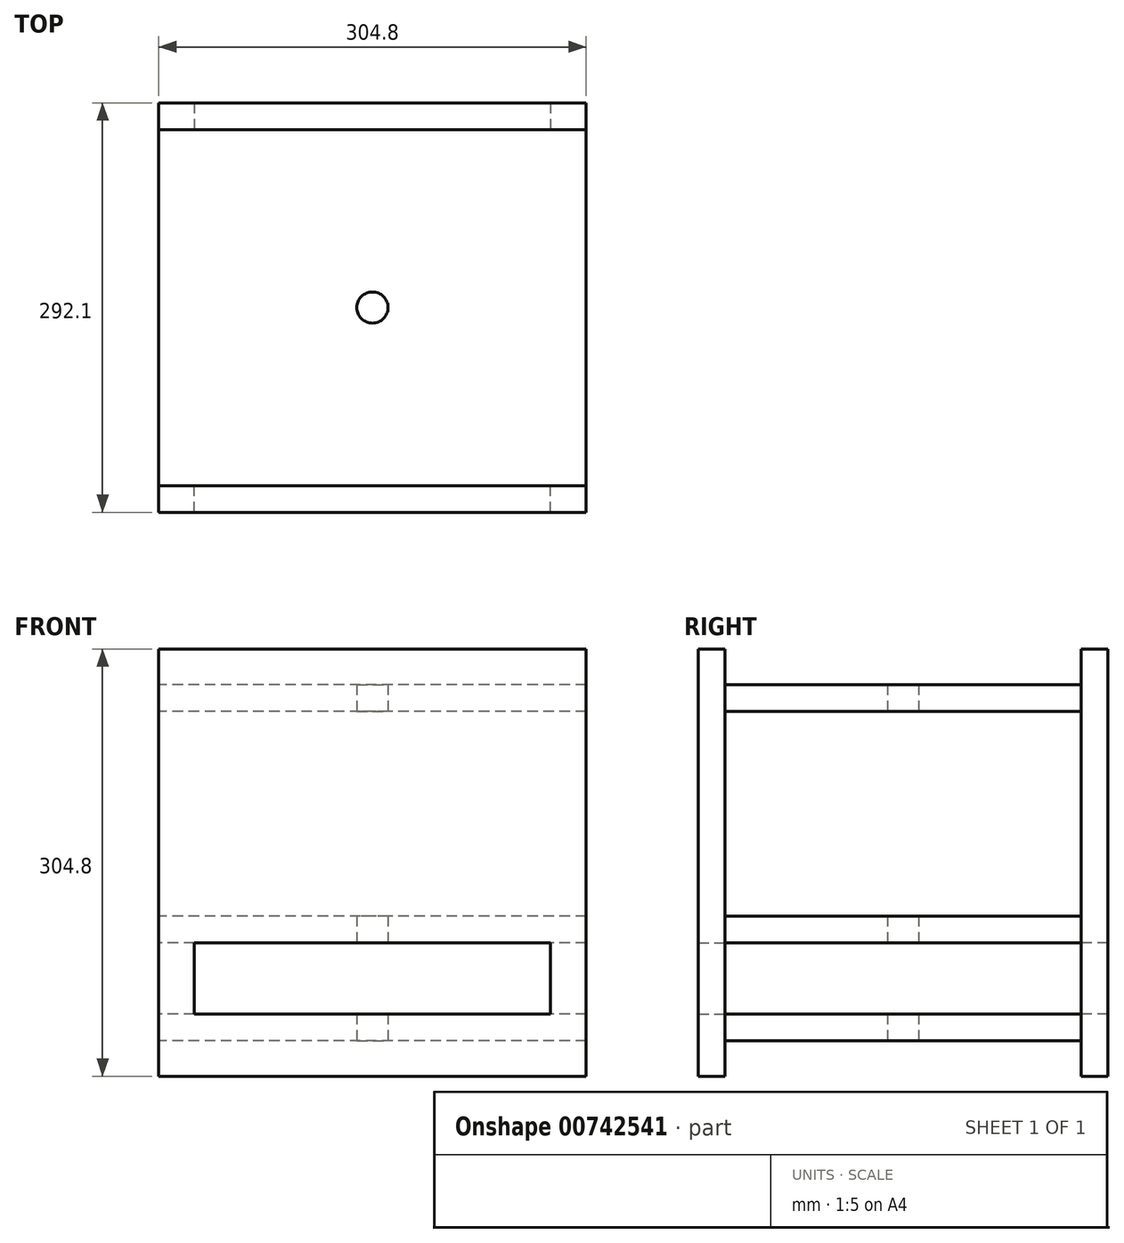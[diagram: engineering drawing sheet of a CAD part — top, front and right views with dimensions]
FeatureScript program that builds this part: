
annotation { "Feature Type Name" : "Feature", "Feature Type Description" : "" }
export const myFeature = defineFeature(function(context is Context, id is Id, definition is map)
    precondition{}
    {
        {
            var Q0;
            Q0=qCreatedBy(makeId("Right.planeOp"),FACE);
            var sketch = newSketch(context, id + "F0", { "sketchPlane" : qUnion([Q0])});
            skLineSegment(sketch, "E0", {"start": v(0, 130.28) * mm, "end": v(254, 130.28) * mm});
            skLineSegment(sketch, "E1", {"start": v(0, 111.23) * mm, "end": v(254, 111.23) * mm});
            skLineSegment(sketch, "E2", {"start": v(254, 130.28) * mm, "end": v(254, 111.23) * mm});
            skLineSegment(sketch, "E3", {"start": v(0, -34.82) * mm, "end": v(254, -34.82) * mm});
            skLineSegment(sketch, "E4", {"start": v(0, -53.87) * mm, "end": v(254, -53.87) * mm});
            skLineSegment(sketch, "E5", {"start": v(0, -104.67) * mm, "end": v(254, -104.67) * mm});
            skLineSegment(sketch, "E6", {"start": v(0, -123.72) * mm, "end": v(254, -123.72) * mm});
            skLineSegment(sketch, "E7", {"start": v(0, -104.67) * mm, "end": v(0, -123.72) * mm});
            skLineSegment(sketch, "E8", {"start": v(254, -104.67) * mm, "end": v(254, -123.72) * mm});
            skLineSegment(sketch, "E9", {"start": v(254, -34.82) * mm, "end": v(254, -53.87) * mm});
            skLineSegment(sketch, "E10", {"start": v(0, -34.82) * mm, "end": v(0, -53.87) * mm});
            skLineSegment(sketch, "E11", {"start": v(0, 130.28) * mm, "end": v(0, 111.23) * mm});
            skSolve(sketch);
        }
        {
            var Q0;
            Q0 = qSketchRegion(id + "F0", true);
            extrude(context, id + "F1", {"entities" : qUnion([Q0]), "depth" : 304.8 * mm, "offsetDistance" : 25.4 * mm});
        }
        {
            var Q0;
            Q0=makeQuery(id+"F1.opExtrude","SWEPT_FACE",FACE,{"disambiguationData":[OSD([sQuery(id+"F0.wireOp",EDGE,"E8")])]});
            cPlane(context, id + "F2", {"entities" : qUnion([Q0]), "cplaneType" : CPlaneType.OFFSET, "offset" : 0 * mm, "width" : 152.4 * mm, "height" : 152.4 * mm});
        }
        {
            var Q0;
            Q0=qCreatedBy(id+"F2.planeOp",FACE);
            var sketch = newSketch(context, id + "F3", { "sketchPlane" : qUnion([Q0])});
            skLineSegment(sketch, "E12", {"start": v(-279.4, -53.87) * mm, "end": v(-25.4, -53.87) * mm});
            skLineSegment(sketch, "E13", {"start": v(-25.4, -104.67) * mm, "end": v(-25.4, -53.87) * mm});
            skLineSegment(sketch, "E14", {"start": v(-25.4, -104.67) * mm, "end": v(-279.4, -104.67) * mm});
            skLineSegment(sketch, "E15", {"start": v(-279.4, -104.67) * mm, "end": v(-279.4, -53.87) * mm});
            skLineSegment(sketch, "E16", {"start": v(-304.8, -149.12) * mm, "end": v(-304.8, 155.68) * mm});
            skLineSegment(sketch, "E17", {"start": v(-304.8, 155.68) * mm, "end": v(0, 155.68) * mm});
            skLineSegment(sketch, "E18", {"start": v(-304.8, -149.12) * mm, "end": v(0, -149.12) * mm});
            skLineSegment(sketch, "E19", {"start": v(0, -149.12) * mm, "end": v(0, 155.68) * mm});
            skSolve(sketch);
        }
        {
            var Q0;
            Q0=makeQuery(id+"F1.opExtrude","SWEPT_FACE",FACE,{"disambiguationData":[OSD([sQuery(id+"F0.wireOp",EDGE,"E11")])]});
            cPlane(context, id + "F4", {"entities" : qUnion([Q0]), "cplaneType" : CPlaneType.OFFSET, "offset" : 0 * mm, "width" : 152.4 * mm, "height" : 152.4 * mm});
        }
        {
            var Q0;
            Q0 = qSketchRegion(id + "F3", true);
            extrude(context, id + "F5", {"entities" : qUnion([Q0]), "depth" : 19.05 * mm, "offsetDistance" : 25.4 * mm});
        }
        {
            var Q0;
            Q0=qCreatedBy(id+"F4.planeOp",FACE);
            var sketch = newSketch(context, id + "F6", { "sketchPlane" : qUnion([Q0])});
            skLineSegment(sketch, "E20", {"start": v(0, 155.68) * mm, "end": v(0, -149.12) * mm});
            skLineSegment(sketch, "E21", {"start": v(0, 155.68) * mm, "end": v(304.8, 155.68) * mm});
            skLineSegment(sketch, "E22", {"start": v(304.8, 155.68) * mm, "end": v(304.8, -149.12) * mm});
            skLineSegment(sketch, "E23", {"start": v(0, -149.12) * mm, "end": v(304.8, -149.12) * mm});
            skLineSegment(sketch, "E24", {"start": v(25.4, -53.87) * mm, "end": v(279.4, -53.87) * mm});
            skLineSegment(sketch, "E25", {"start": v(279.4, -53.87) * mm, "end": v(279.4, -104.67) * mm});
            skLineSegment(sketch, "E26", {"start": v(279.4, -104.67) * mm, "end": v(25.4, -104.67) * mm});
            skLineSegment(sketch, "E27", {"start": v(25.4, -104.67) * mm, "end": v(25.4, -53.87) * mm});
            skSolve(sketch);
        }
        {
            var Q0;
            Q0=makeQuery(id+"F6.imprint","IMPRINT",FACE,{"disambiguationData":[TD([[makeQuery(id+"F6.imprint","IMPRINT",EDGE,{"derivedFrom":sQuery(id+"F6.wireOp",EDGE,"E20")}),1.0]])]});
            extrude(context, id + "F7", {"entities" : qUnion([Q0]), "depth" : 19.05 * mm, "offsetDistance" : 25.4 * mm});
        }
        {
            var Q0;
            Q0=makeQuery(id+"F1.opExtrude","SWEPT_FACE",FACE,{"disambiguationData":[OSD([sQuery(id+"F0.wireOp",EDGE,"E6")])]});
            var sketch = newSketch(context, id + "F8", { "sketchPlane" : qUnion([Q0])});
            skCircle(sketch, "E28", {"center": v(152.4, -127) * mm, "radius": 11.11 * mm});
            skSolve(sketch);
        }
        {
            var Q0;
            Q0 = qSketchRegion(id + "F8", true);
            extrude(context, id + "F9", {"entities" : qUnion([Q0]), "operationType" : NewBodyOperationType.REMOVE, "oppositeDirection" : true, "depth" : 254 * mm, "offsetDistance" : 25.4 * mm});
        }
    });
